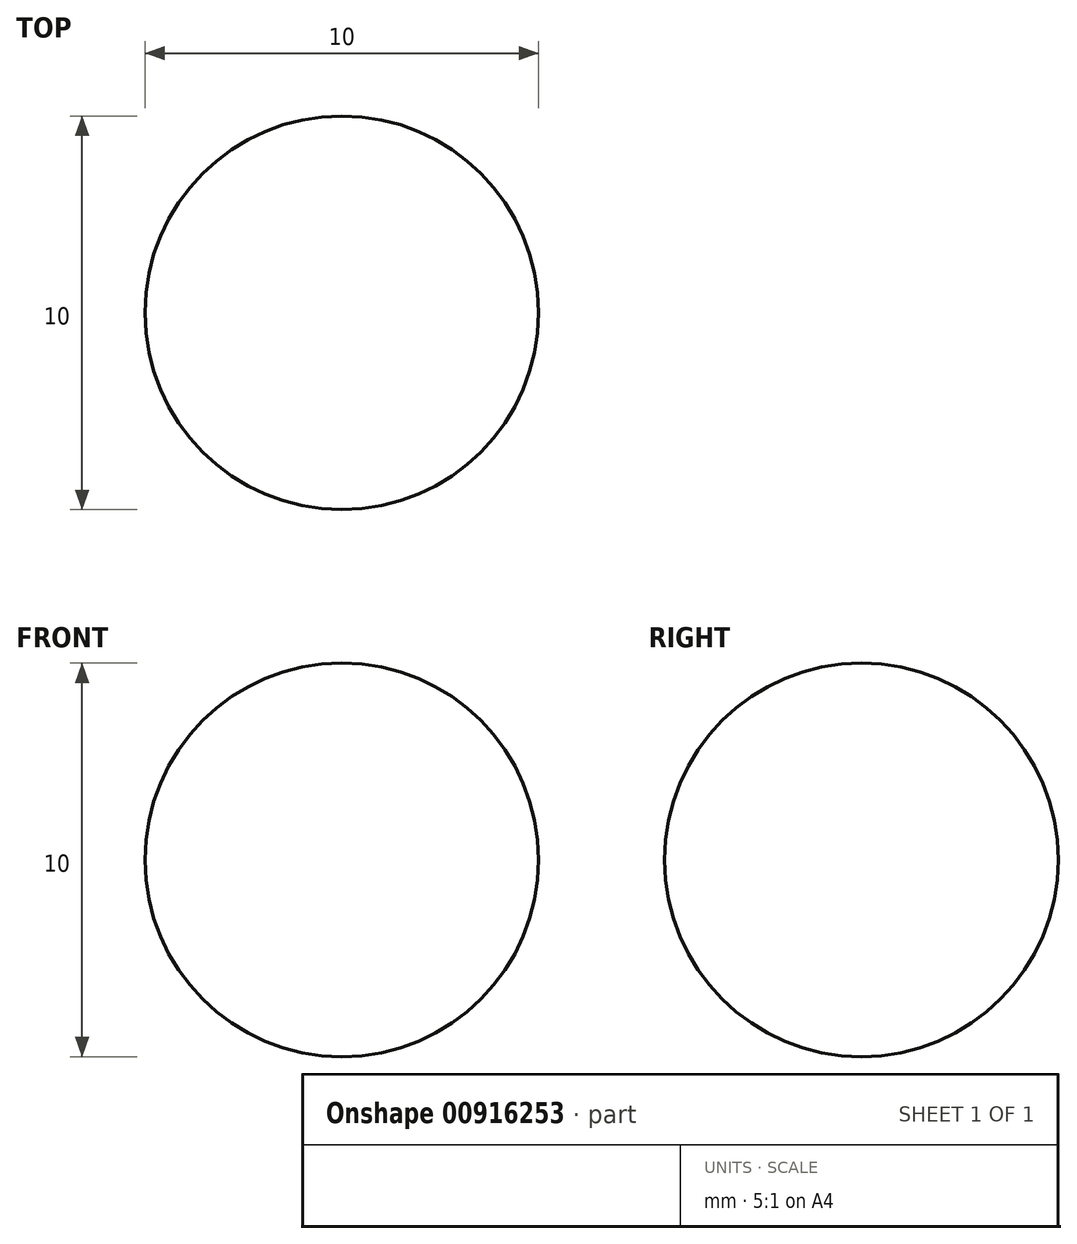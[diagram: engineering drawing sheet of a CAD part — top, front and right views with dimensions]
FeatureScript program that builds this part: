
annotation { "Feature Type Name" : "Feature", "Feature Type Description" : "" }
export const myFeature = defineFeature(function(context is Context, id is Id, definition is map)
    precondition{}
    {
        {
            var Q0;
            Q0=qCreatedBy(makeId("Front.planeOp"),FACE);
            var sketch = newSketch(context, id + "F0", { "sketchPlane" : qUnion([Q0])});
            skLineSegment(sketch, "E0", {"start": v(0, 0) * mm, "end": v(0, 10) * mm});
            skArc(sketch, "E1", {"start": v(0, 10) * mm, "mid": v(5, 5) * mm, "end": v(0, 0) * mm});
            skSolve(sketch);
        }
        {
            var Q0;
            Q0 = qSketchRegion(id + "F0", true);
            var Q1;
            Q1=sQuery(id+"F0.wireOp",EDGE,"E0");
            revolve(context, id + "F1", {"surfaceOperationType" : NewSurfaceOperationType.NEW, "entities" : qUnion([Q0]), "axis" : qUnion([Q1]), "revolveType" : RevolveType.FULL});
        }
    });
